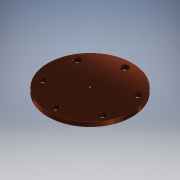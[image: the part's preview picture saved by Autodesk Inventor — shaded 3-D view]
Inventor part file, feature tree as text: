
AUTODESK INVENTOR PART (.ipt)
format: ipt  version: 2017.3 (Build 213256000, 256)  size: 205,824 bytes
history: native  units: mm
features: sketch x3, extrude x2, move_body x1
ambient origin geometry x8: Origin, YZ Plane, XZ Plane, XY Plane, X Axis, Y Axis, Z Axis, Center Point
bodies: Solid1 (feature_tree)
feature tree (6):
  extrude  "Extrusion1"  Depth=1.0mm TaperAngle=0.0deg
  extrude  "Extrusion2"  Depth=1.0mm
  move_body  "Move Body1"
  sketch  "Sketch3"  dims[d5=1.67mm d6=1.67mm d7=1.67mm d8=1.67mm d9=1.67mm d10=1.0mm d11=0.0mm d12=90.0deg]
  sketch  "Sketch1"  dims[d0=19.0mm d1=1.0mm d2=0.0mm]
  sketch  "Sketch2"  dims[d3=1.0mm d4=1.67mm]
